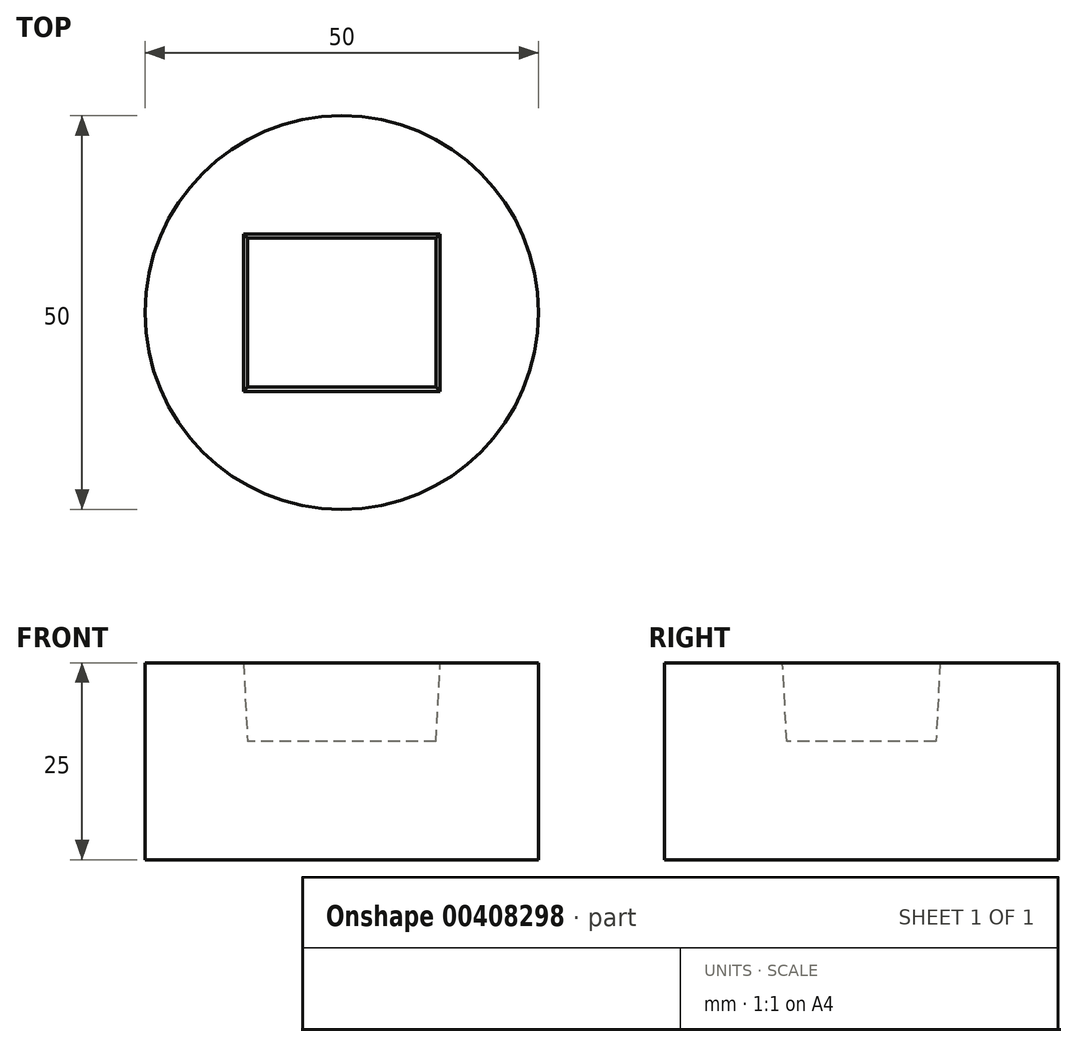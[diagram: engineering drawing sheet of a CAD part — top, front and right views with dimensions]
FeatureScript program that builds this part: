
annotation { "Feature Type Name" : "Feature", "Feature Type Description" : "" }
export const myFeature = defineFeature(function(context is Context, id is Id, definition is map)
    precondition{}
    {
        {
            var Q0;
            Q0=qCreatedBy(makeId("Top.planeOp"),FACE);
            var sketch = newSketch(context, id + "F0", { "sketchPlane" : qUnion([Q0])});
            skCircle(sketch, "E0", {"center": v(0, 0) * mm, "radius": 25 * mm});
            skSolve(sketch);
        }
        {
            var Q0;
            Q0 = qSketchRegion(id + "F0", true);
            extrude(context, id + "F1", {"entities" : qUnion([Q0]), "depth" : 25 * mm});
        }
        {
            var Q0;
            Q0=makeQuery(id+"F1.opExtrude","CAP_FACE",FACE,{"disambiguationData":[OSD([sQuery(id+"F0.wireOp",EDGE,"E0")])],"isStart":false});
            var sketch = newSketch(context, id + "F2", { "sketchPlane" : qUnion([Q0])});
            skLineSegment(sketch, "E1", {"start": v(-39.22, 0) * mm, "end": v(42.8, 0) * mm, "construction": true});
            skLineSegment(sketch, "E2", {"start": v(0, 38.62) * mm, "end": v(0, -30.82) * mm, "construction": true});
            skLineSegment(sketch, "E3.bottom", {"start": v(-12.5, 10) * mm, "end": v(12.5, 10) * mm});
            skLineSegment(sketch, "E3.top", {"start": v(-12.5, -10) * mm, "end": v(12.5, -10) * mm});
            skLineSegment(sketch, "E3.left", {"start": v(-12.5, 10) * mm, "end": v(-12.5, -10) * mm});
            skLineSegment(sketch, "E3.right", {"start": v(12.5, 10) * mm, "end": v(12.5, -10) * mm});
            skSolve(sketch);
        }
        {
            var Q0;
            Q0 = qSketchRegion(id + "F2", true);
            extrude(context, id + "F3", {"entities" : qUnion([Q0]), "operationType" : NewBodyOperationType.REMOVE, "oppositeDirection" : true, "depth" : 10 * mm, "hasDraft" : true, "draftAngle" : 3 * degree, "draftPullDirection" : true});
        }
    });
